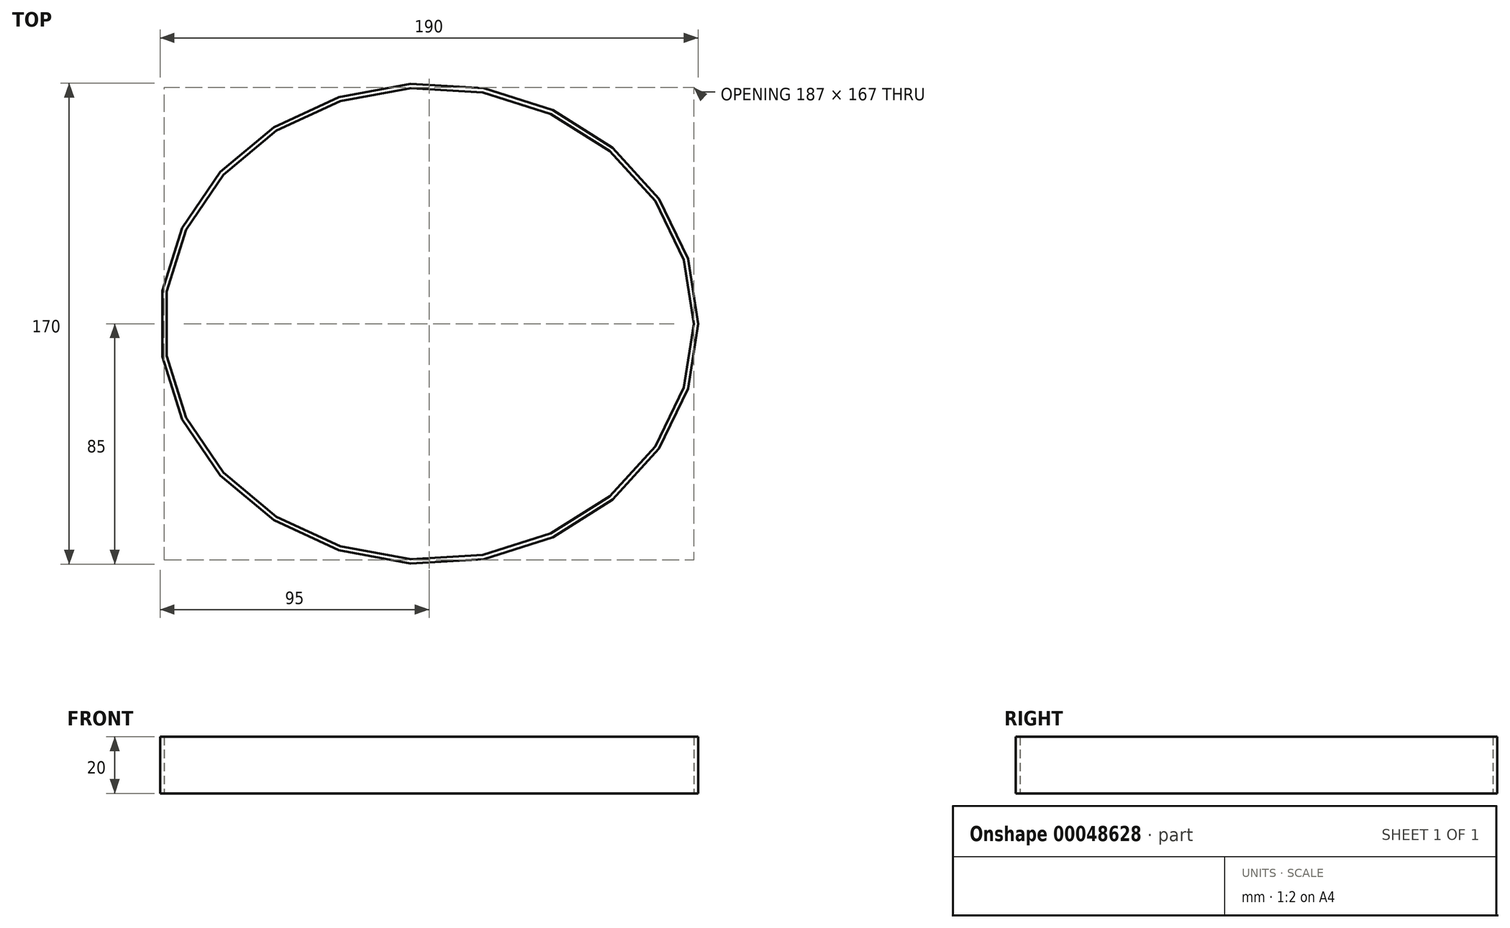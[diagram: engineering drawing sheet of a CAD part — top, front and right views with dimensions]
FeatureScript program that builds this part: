
annotation { "Feature Type Name" : "Feature", "Feature Type Description" : "" }
export const myFeature = defineFeature(function(context is Context, id is Id, definition is map)
    precondition{}
    {
        {
            var Q0;
            Q0=qCreatedBy(makeId("Top.planeOp"),FACE);
            var sketch = newSketch(context, id + "F0", { "sketchPlane" : qUnion([Q0])});
            skEllipse(sketch, "E0", {"center": v(0, 0) * mm, "majorRadius": 95 * mm, "minorRadius": 85 * mm, "majorAxis": v(1, 0)});
            skEllipse(sketch, "E1", {"center": v(0, 0) * mm, "majorRadius": 93.5 * mm, "minorRadius": 83.5 * mm, "majorAxis": v(1, 0)});
            skSolve(sketch);
        }
        {
            var Q0;
            Q0 = qSketchRegion(id + "F0", true);
            extrude(context, id + "F1", {"entities" : qUnion([Q0]), "depth" : 20 * mm});
        }
    });
